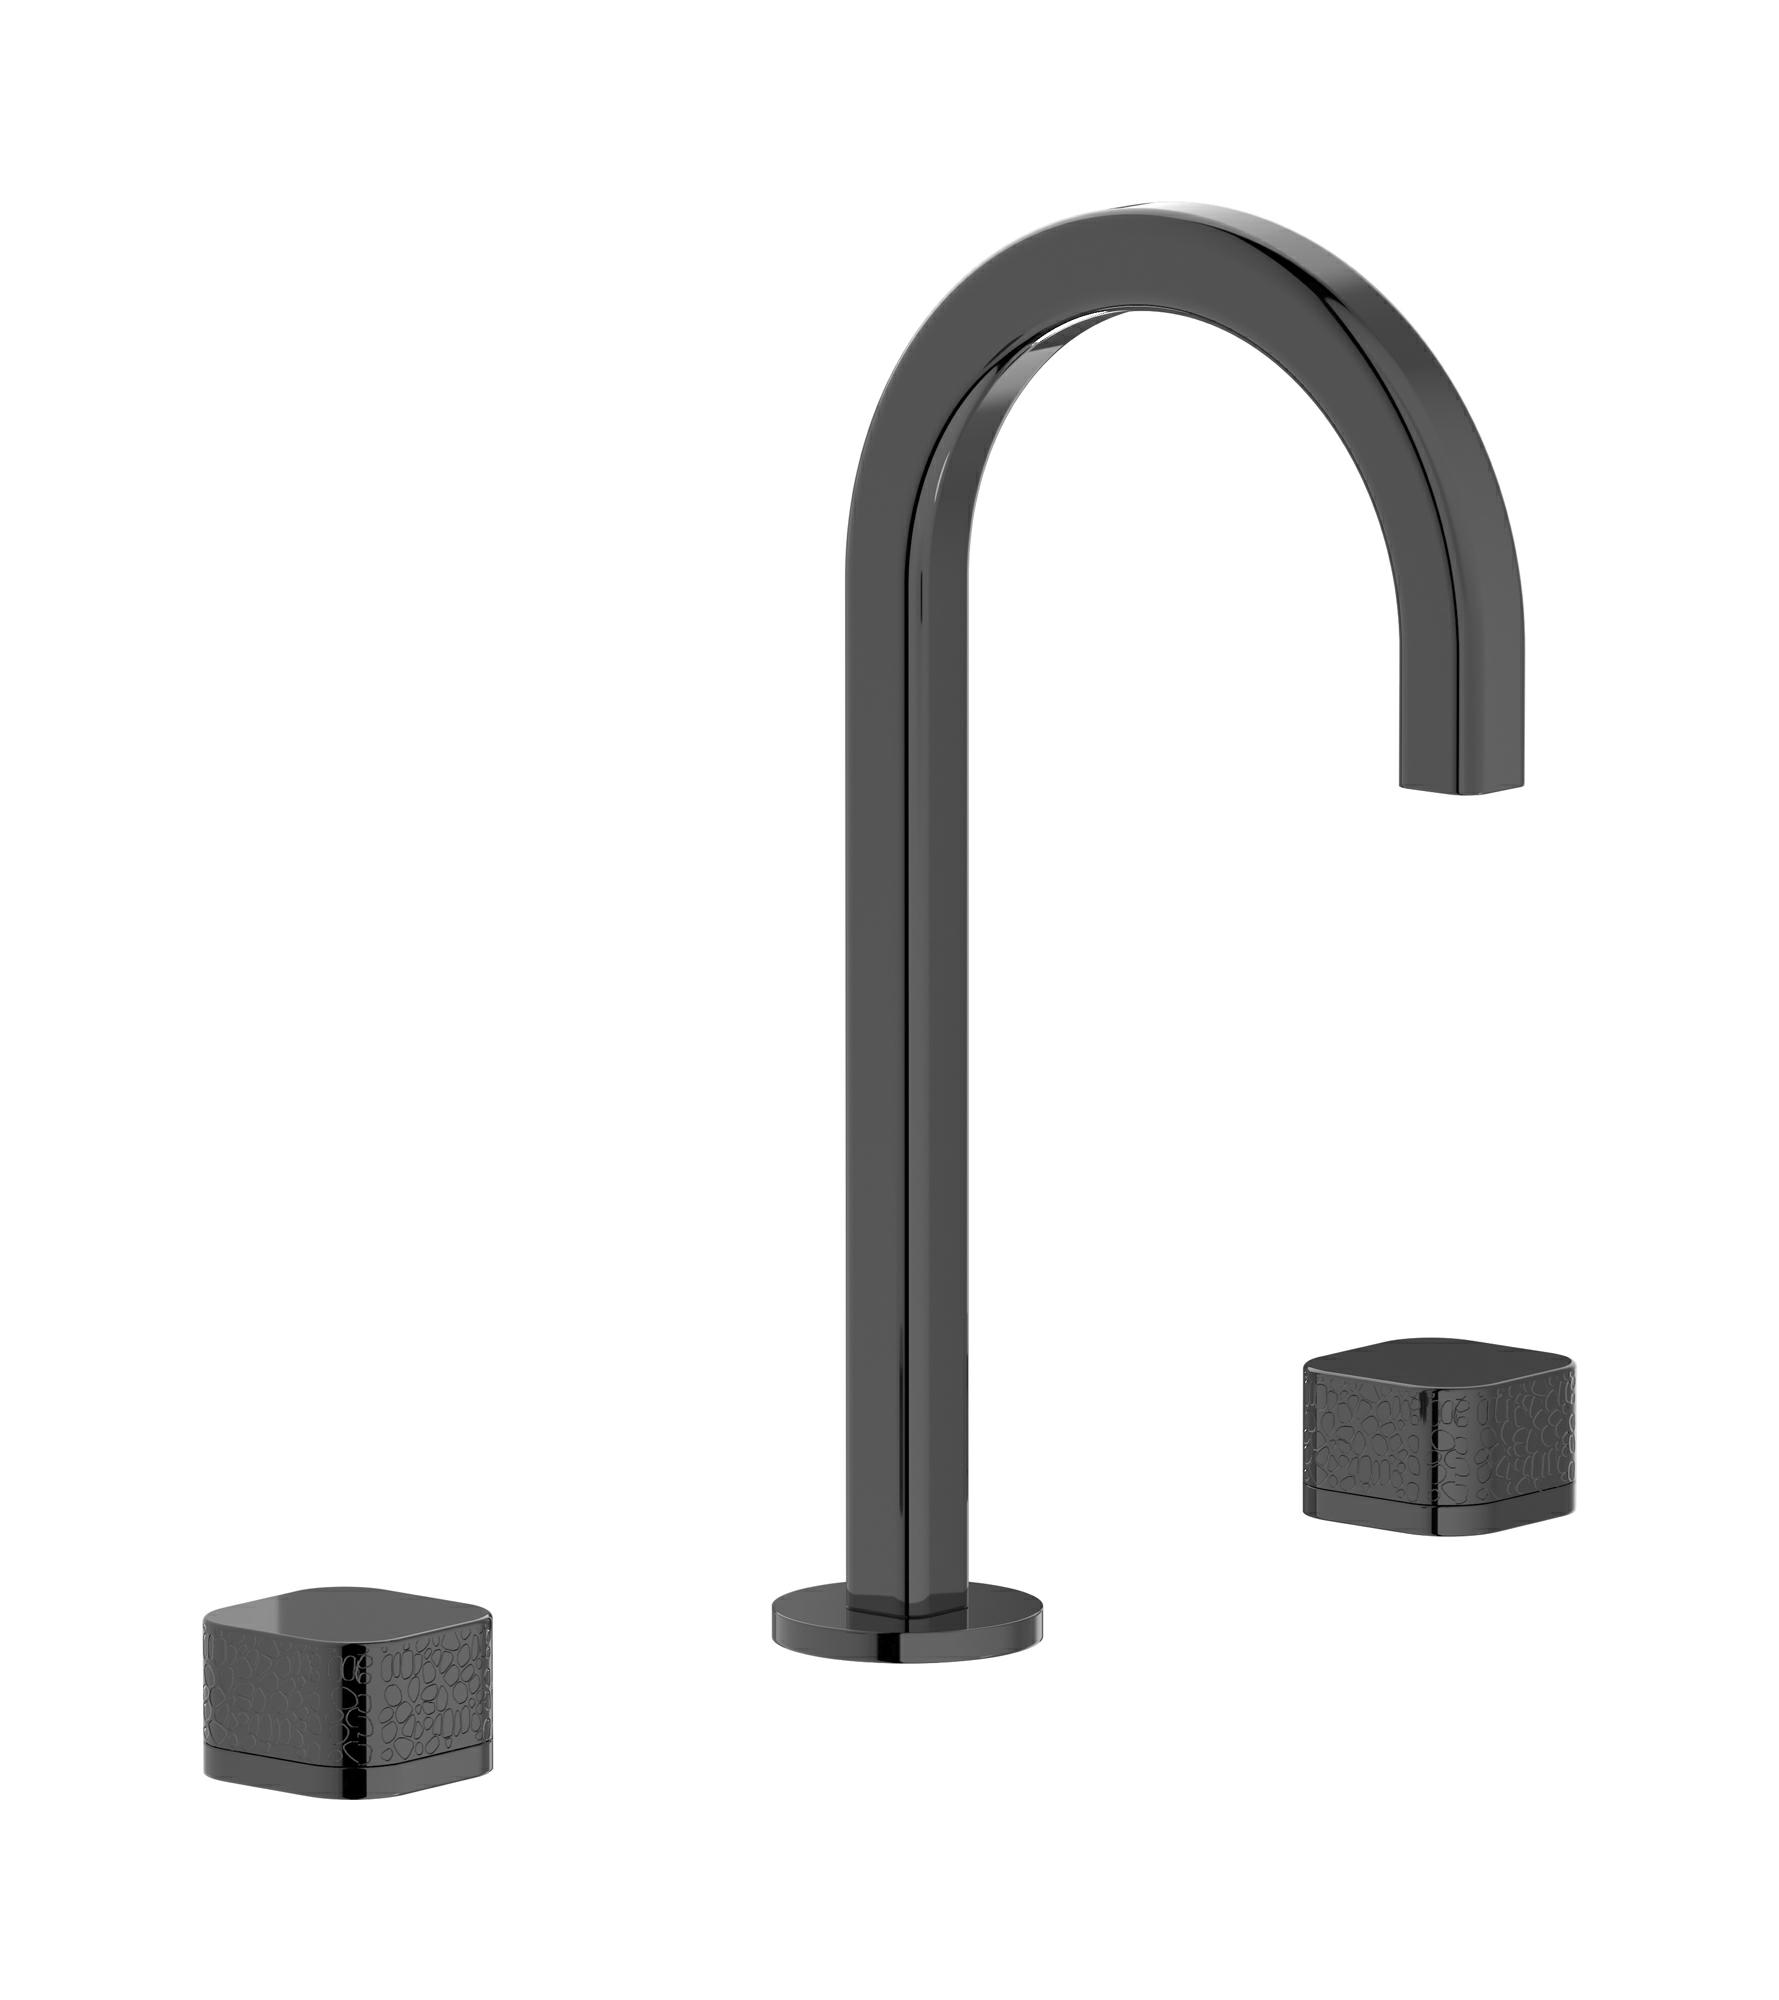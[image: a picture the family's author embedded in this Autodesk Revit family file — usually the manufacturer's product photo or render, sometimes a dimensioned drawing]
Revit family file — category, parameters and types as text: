
# Revit family: EO392_4
name_source: partatom
category: Apparecchi idraulici
units: mm (PartAtom-declared; Revit-internal decimal feet)

## family parameters
Basato su piano di lavoro = No
Condiviso = No
Mantieni orientamento annotazione = No
Numero OmniClass = 23.45.55.17
Punto di calcolo locali = No
Quota connettore circolare = Usa diametro
Sempre verticale = Sì
Taglio con vuoti quando caricato = No
Tipo di parte = Normale
Titolo OmniClass = Mixing Faucets

## types (12) — shared parameters
Cold water inlet = 10 mm  [stored 0.0328084 ft]
Commenti sul tipo = Washbasin
Connessione CW = No
Connessione HW = No
Connessione di scarico = No
Connessione di ventilazione = No
Descrizione = Three hole washbasin complete
Hot water inlet = 10 mm  [stored 0.0328084 ft]
Produttore = IB Rubinetterie S.p.A.
URL = https://www.weareib.it
zero-valued in all types: Prospetto di default

## per-type parameters (varying)
| type | Finishes surface | Immagine tipo | Modello |
| Chrome | IB_Chrome | EO392CC_4.jpg | EO392CC_4 |
| Brushed nickel | IB_Brushed nickel | EO392SS_4.jpg | EO392SS_4 |
| Natural brass | IB_Brass | EO392ON_4.jpg | EO392ON_4 |
| Matt black | IB_matt black | EO392NP_4.jpg | EO392NP_4 |
| Black chrome | IB_Black chrome | EO392CF_4.jpg | EO392CF_4 |
| Brushed black chrome | IB_Brushed black chrome | EO392CS_4.jpg | EO392CS_4 |
| Pale gold | IB_Pale gold | EO392II_4.jpg | EO392II_4 |
| Brushed pale gold | IB_brushed pale gold | EO392IS_4.jpg | EO392IS_4 |
| Rose gold | IB_Rose gold | EO392RS_4.jpg | EO392RS_4 |
| Brushed rose gold | IB_Brushed rose gold | EO392SR_4.jpg | EO392SR_4 |
| Gold | IB_gold | EO392OO_4.jpg | EO392OO_4 |
| Brushed gold | IB_brushed gold | EO392OS_4.jpg | EO392OS_4 |

note: [stored X ft] marks values corroborated as IEEE doubles in the binary element streams (Revit-internal decimal feet)
